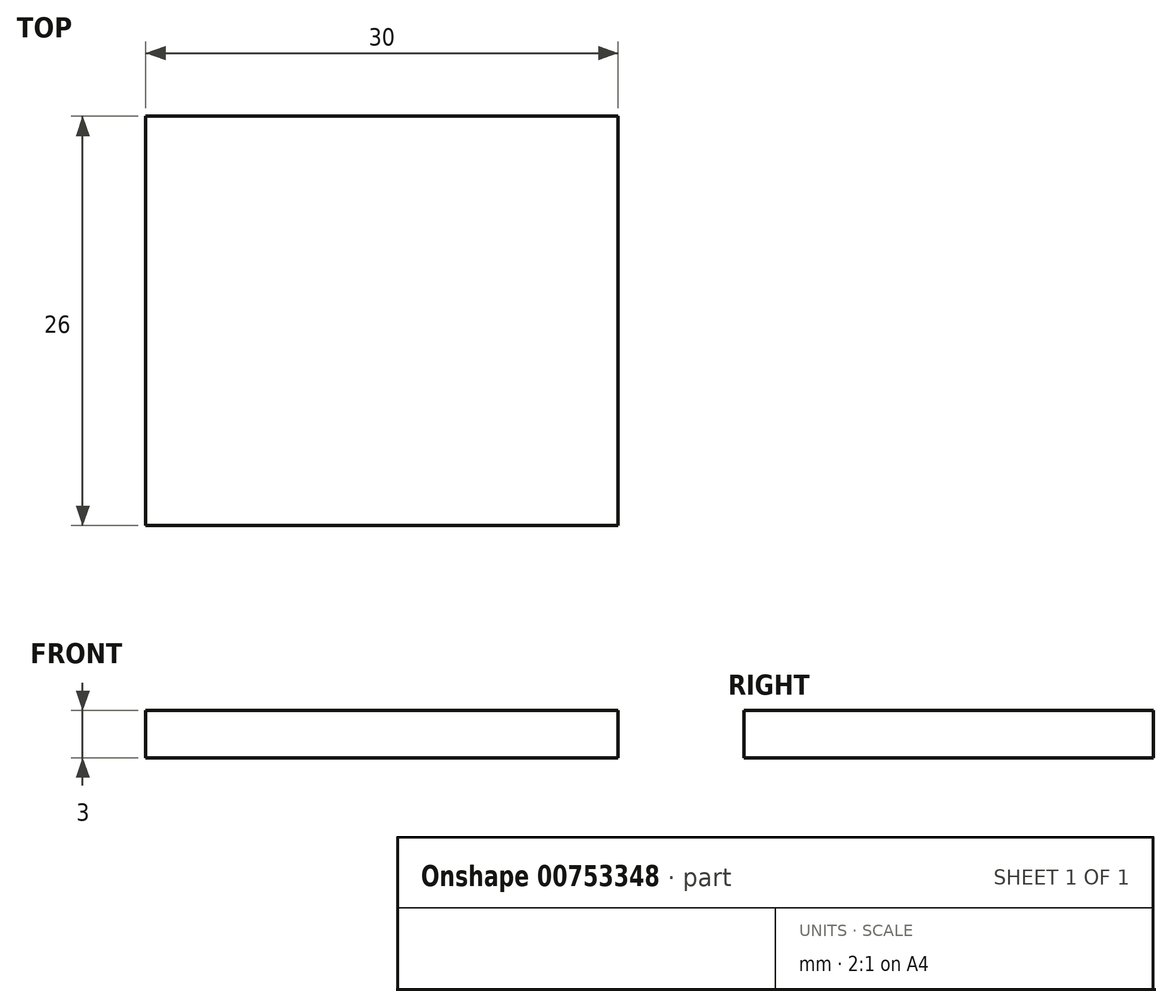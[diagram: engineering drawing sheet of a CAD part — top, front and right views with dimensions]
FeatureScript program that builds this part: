
annotation { "Feature Type Name" : "Feature", "Feature Type Description" : "" }
export const myFeature = defineFeature(function(context is Context, id is Id, definition is map)
    precondition{}
    {
        {
            var Q0;
            Q0=qCreatedBy(makeId("Top.planeOp"),FACE);
            var sketch = newSketch(context, id + "F0", { "sketchPlane" : qUnion([Q0])});
            skLineSegment(sketch, "E0.bottom", {"start": v(15, 13) * mm, "end": v(-15, 13) * mm});
            skLineSegment(sketch, "E0.top", {"start": v(15, -13) * mm, "end": v(-15, -13) * mm});
            skLineSegment(sketch, "E0.left", {"start": v(15, 13) * mm, "end": v(15, -13) * mm});
            skLineSegment(sketch, "E0.right", {"start": v(-15, 13) * mm, "end": v(-15, -13) * mm});
            skPoint(sketch, "E0.middle", {"position": v(0, 0) * mm});
            skSolve(sketch);
        }
        {
            var Q0;
            Q0 = qSketchRegion(id + "F0", true);
            extrude(context, id + "F1", {"entities" : qUnion([Q0]), "depth" : 3 * mm, "offsetDistance" : 25 * mm});
        }
    });
